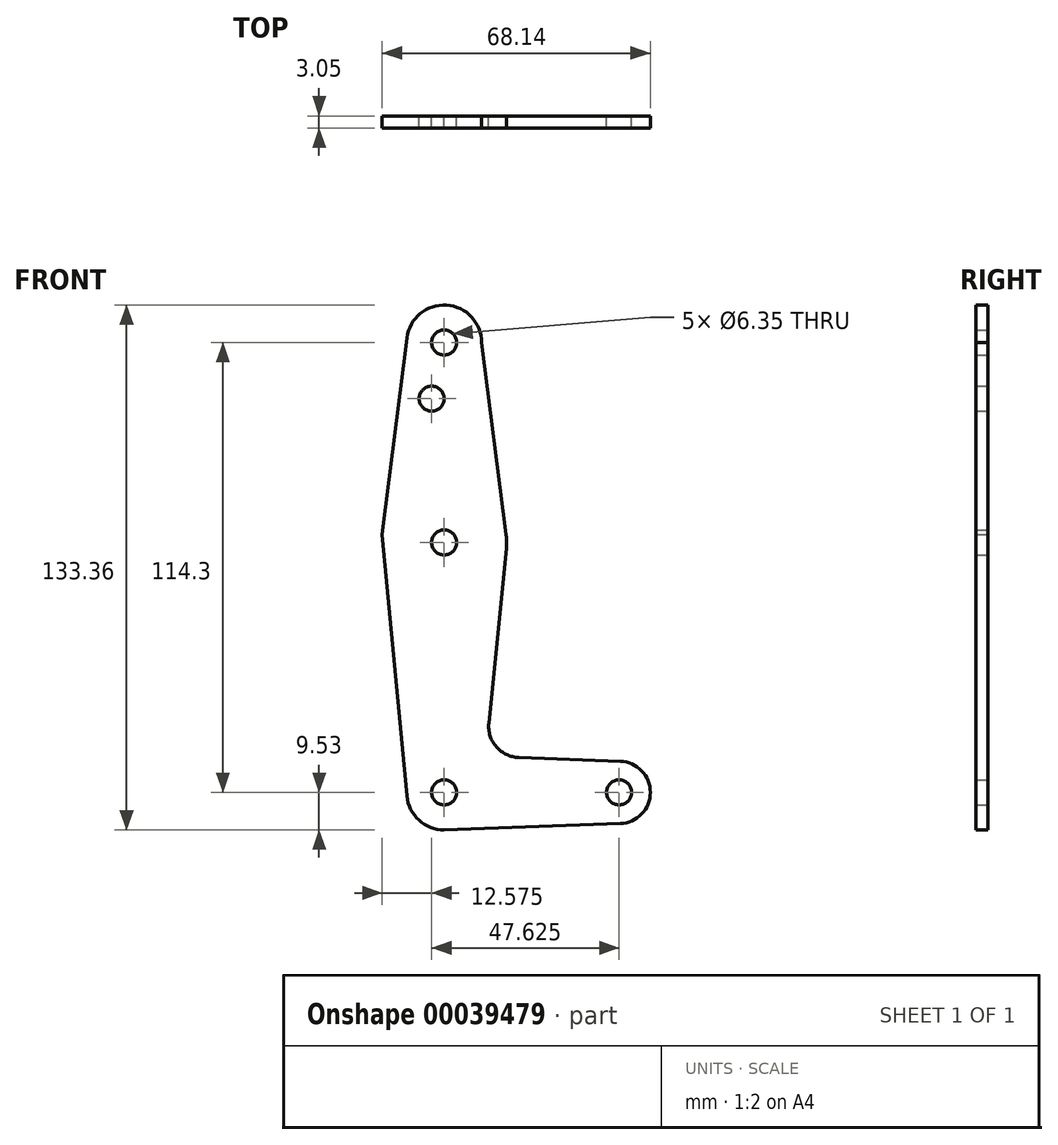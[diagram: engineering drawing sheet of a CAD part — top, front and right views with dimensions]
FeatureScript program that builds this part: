
annotation { "Feature Type Name" : "Feature", "Feature Type Description" : "" }
export const myFeature = defineFeature(function(context is Context, id is Id, definition is map)
    precondition{}
    {
        {
            var Q0;
            Q0=qCreatedBy(makeId("Front.planeOp"),FACE);
            var sketch = newSketch(context, id + "F0", { "sketchPlane" : qUnion([Q0])});
            skLineSegment(sketch, "E0", {"start": v(0, 0) * mm, "end": v(0, 114.3) * mm, "construction": true});
            skLineSegment(sketch, "E1", {"start": v(0, 0) * mm, "end": v(44.45, 0) * mm, "construction": true});
            skCircle(sketch, "E2", {"center": v(0, 114.3) * mm, "radius": 9.53 * mm});
            skCircle(sketch, "E3", {"center": v(0, 0) * mm, "radius": 9.53 * mm});
            skCircle(sketch, "E4", {"center": v(44.45, 0) * mm, "radius": 7.94 * mm});
            skCircle(sketch, "E5", {"center": v(0, 63.5) * mm, "radius": 15.88 * mm});
            skLineSegment(sketch, "E6", {"start": v(-9.45, 115.5) * mm, "end": v(-15.75, 65.48) * mm});
            skLineSegment(sketch, "E7", {"start": v(-15.75, 65.48) * mm, "end": v(-9.48, -0.9) * mm});
            skLineSegment(sketch, "E8", {"start": v(9.52, 114.3) * mm, "end": v(15.75, 65.5) * mm});
            skLineSegment(sketch, "E9", {"start": v(0, -9.53) * mm, "end": v(44.73, -7.93) * mm});
            skCircle(sketch, "E10", {"center": v(0, 63.5) * mm, "radius": 3.18 * mm});
            skCircle(sketch, "E11", {"center": v(0, 114.3) * mm, "radius": 3.18 * mm});
            skCircle(sketch, "E12", {"center": v(0, 0) * mm, "radius": 3.18 * mm});
            skCircle(sketch, "E13", {"center": v(44.45, 0) * mm, "radius": 3.18 * mm});
            skCircle(sketch, "E14", {"center": v(-3.18, 100.03) * mm, "radius": 3.18 * mm});
            skArc(sketch, "E15.filletArc", {"start": v(11.34, 17.6) * mm, "mid": v(13.26, 11.57) * mm, "end": v(18.97, 8.85) * mm});
            skLineSegment(sketch, "E16", {"start": v(18.97, 8.85) * mm, "end": v(44.73, 7.93) * mm});
            skLineSegment(sketch, "E17", {"start": v(11.34, 17.6) * mm, "end": v(15.8, 61.91) * mm});
            skSolve(sketch);
        }
        {
            var Q0;
            {var subQ2=sQuery(id+"F0.wireOp",EDGE,"E6");Q0=makeQuery(id+"F0.imprint","IMPRINT",FACE,{"disambiguationData":[TD([[makeQuery(id+"F0.imprint","IMPRINT",EDGE,{"derivedFrom":subQ2}),1.0]])]});}
            var Q1;
            Q1=makeQuery(id+"F0.imprint","IMPRINT",FACE,{"disambiguationData":[TD([[makeQuery(id+"F0.imprint","IMPRINT",EDGE,{"derivedFrom":sQuery(id+"F0.wireOp",EDGE,"E10")}),-1.0]])]});
            var Q2;
            Q2=makeQuery(id+"F0.imprint","IMPRINT",FACE,{"disambiguationData":[TD([[makeQuery(id+"F0.imprint","IMPRINT",EDGE,{"derivedFrom":sQuery(id+"F0.wireOp",EDGE,"E15.filletArc")}),-1.0]])]});
            var Q3;
            Q3=makeQuery(id+"F0.imprint","IMPRINT",FACE,{"disambiguationData":[TD([[makeQuery(id+"F0.imprint","IMPRINT",EDGE,{"derivedFrom":sQuery(id+"F0.wireOp",EDGE,"E12")}),-1.0]])]});
            var Q4;
            Q4=makeQuery(id+"F0.imprint","IMPRINT",FACE,{"disambiguationData":[TD([[makeQuery(id+"F0.imprint","IMPRINT",EDGE,{"derivedFrom":sQuery(id+"F0.wireOp",EDGE,"E13")}),-1.0]])]});
            var Q5;
            Q5=makeQuery(id+"F0.imprint","IMPRINT",FACE,{"disambiguationData":[TD([[makeQuery(id+"F0.imprint","IMPRINT",EDGE,{"derivedFrom":sQuery(id+"F0.wireOp",EDGE,"E11")}),-1.0]])]});
            extrude(context, id + "F1", {"entities" : qUnion([Q0, Q1, Q2, Q3, Q4, Q5]), "depth" : 3.05 * mm});
        }
    });
